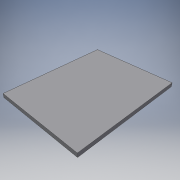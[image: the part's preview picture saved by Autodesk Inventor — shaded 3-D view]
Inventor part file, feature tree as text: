
AUTODESK INVENTOR PART (.ipt)
format: ipt  version: 2016 (Build 200138000, 138)  size: 99,328 bytes
history: native  units: in
note: dims shown in document units (in); Inventor stores cm internally (conversion verified against a paired STEP export)
features: sketch x2, extrude x1
ambient origin geometry x8: Origin, YZ Plane, XZ Plane, XY Plane, X Axis, Y Axis, Z Axis, Center Point
bodies: Solid1 (feature_tree)
feature tree (3):
  extrude  "Extrusion1"  Depth=20.0in
  sketch  "Sketch2"  dims[d2=0.75in d3=0.0in d4=6.0in d5=8.0in d6=3.9375in d7=3.9375in d9=0.125in d10=0.125in d11=0.125in d12=0.125in]
  sketch  "Sketch1"  dims[d0=16.0in d1=20.0in]
